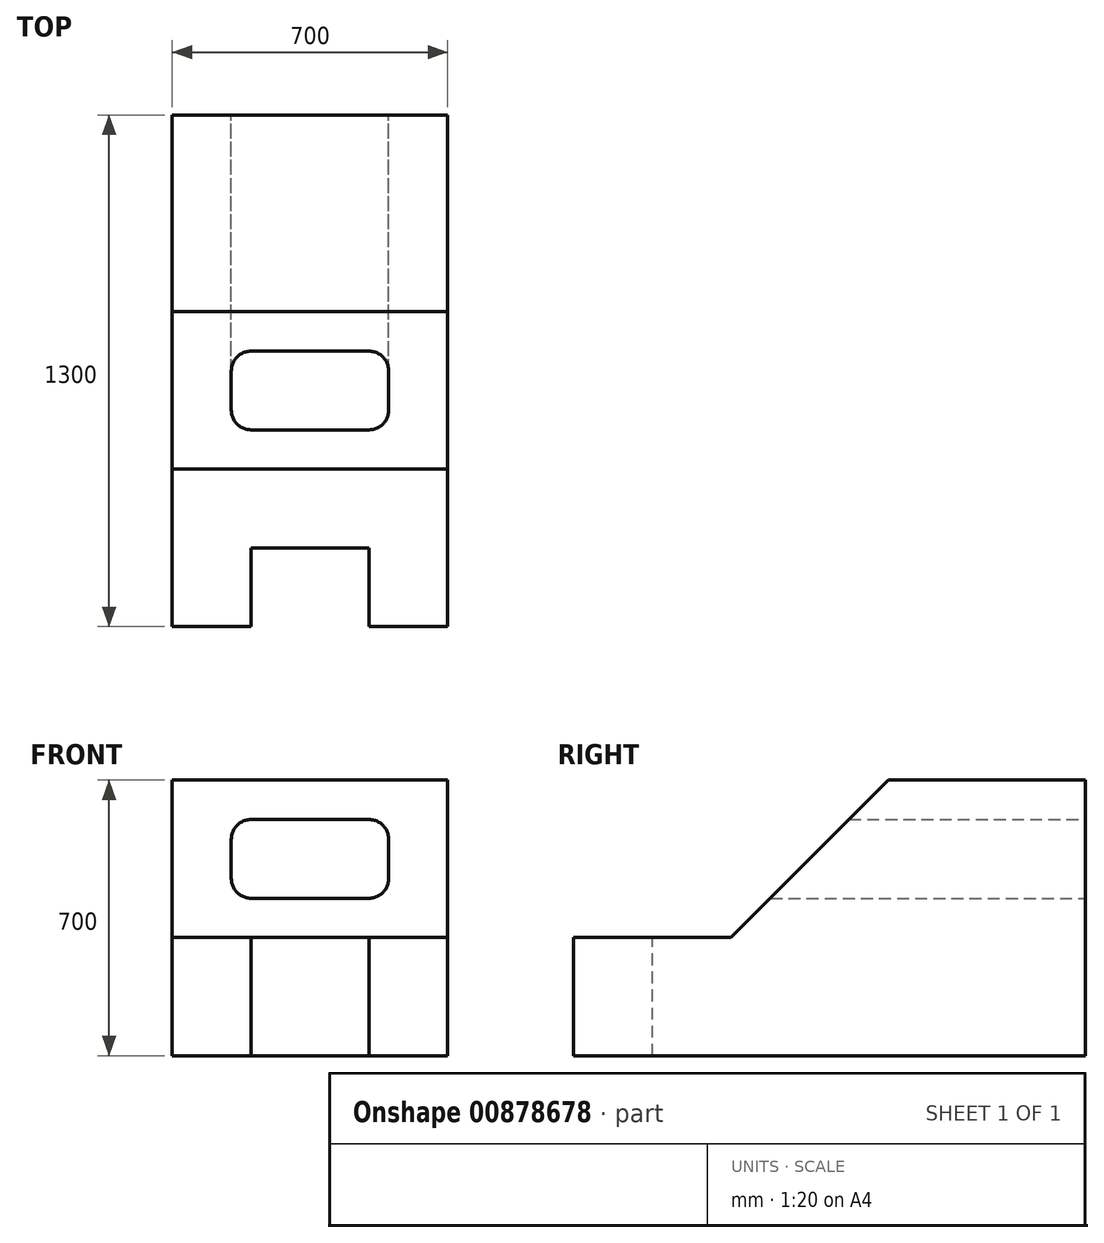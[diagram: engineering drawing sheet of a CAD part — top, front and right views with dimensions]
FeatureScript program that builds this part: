
annotation { "Feature Type Name" : "Feature", "Feature Type Description" : "" }
export const myFeature = defineFeature(function(context is Context, id is Id, definition is map)
    precondition{}
    {
        {
            var Q0;
            Q0=qCreatedBy(makeId("Front.planeOp"),FACE);
            var sketch = newSketch(context, id + "F0", { "sketchPlane" : qUnion([Q0])});
            skLineSegment(sketch, "E0.bottom", {"start": v(350, 350) * mm, "end": v(-350, 350) * mm});
            skLineSegment(sketch, "E0.top", {"start": v(350, -350) * mm, "end": v(-350, -350) * mm});
            skLineSegment(sketch, "E0.left", {"start": v(350, 350) * mm, "end": v(350, -350) * mm});
            skLineSegment(sketch, "E0.right", {"start": v(-350, 350) * mm, "end": v(-350, -350) * mm});
            skPoint(sketch, "E0.middle", {"position": v(0, 0) * mm});
            skSolve(sketch);
        }
        {
            var Q0;
            Q0=makeQuery(id+"F0.imprint","IMPRINT",FACE,{"disambiguationData":[TD([[makeQuery(id+"F0.imprint","IMPRINT",EDGE,{"derivedFrom":sQuery(id+"F0.wireOp",EDGE,"E0.bottom")}),1.0]])]});
            extrude(context, id + "F1", {"entities" : qUnion([Q0]), "depth" : 1300 * mm, "offsetDistance" : 25.4 * mm});
        }
        {
            var Q0;
            Q0=makeQuery(id+"F1.opExtrude","SWEPT_FACE",FACE,{"disambiguationData":[OSD([sQuery(id+"F0.wireOp",EDGE,"E0.left")])]});
            var sketch = newSketch(context, id + "F2", { "sketchPlane" : qUnion([Q0])});
            skLineSegment(sketch, "E1", {"start": v(-500, 350) * mm, "end": v(-900, -50) * mm});
            skLineSegment(sketch, "E2", {"start": v(-900, -50) * mm, "end": v(-1300, -50) * mm});
            skSolve(sketch);
        }
        {
            var Q0;
            {var subQ0=sQuery(id+"F2.wireOp",EDGE,"E1");Q0=makeQuery(id+"F2.imprint","IMPRINT",FACE,{"disambiguationData":[TD([[makeQuery(id+"F2.imprint","IMPRINT",EDGE,{"derivedFrom":subQ0}),-1.0]])]});}
            extrude(context, id + "F3", {"entities" : qUnion([Q0]), "operationType" : NewBodyOperationType.ADD, "endBound" : BoundingType.THROUGH_ALL, "depth" : 25.4 * mm, "offsetDistance" : 25.4 * mm});
        }
        {
            var Q0;
            Q0=makeQuery(id+"F3.opExtrude","CAP_FACE",FACE,{"disambiguationData":[OSD([sQuery(id+"F0.wireOp",EDGE,"E0.bottom"),sQuery(id+"F0.wireOp",EDGE,"E0.left"),sQuery(id+"F2.wireOp",EDGE,"E1"),sQuery(id+"F2.wireOp",EDGE,"E2")])],"isStart":false});
            extrude(context, id + "F4", {"entities" : qUnion([Q0]), "operationType" : NewBodyOperationType.ADD, "endBound" : BoundingType.THROUGH_ALL, "depth" : 25.4 * mm, "offsetDistance" : 25.4 * mm});
        }
        {
            var Q0;
            Q0=makeQuery(id+"F4.opExtrude","CAP_FACE",FACE,{"disambiguationData":[OSD([sQuery(id+"F0.wireOp",EDGE,"E0.bottom"),sQuery(id+"F0.wireOp",EDGE,"E0.left"),sQuery(id+"F2.wireOp",EDGE,"E1"),sQuery(id+"F2.wireOp",EDGE,"E2")])],"isStart":false});
            var sketch = newSketch(context, id + "F5", { "sketchPlane" : qUnion([Q0])});
            skSolve(sketch);
        }
        {
            var Q0;
            Q0 = qSketchRegion(id + "F5", true);
            var Q1;
            Q1=makeQuery(id+"F5.imprint","IMPRINT",FACE,{"disambiguationData":[TD([[makeQuery(id+"F5.imprint","IMPRINT",EDGE,{"derivedFrom":makeQuery(id+"F4.opExtrude","CAP_EDGE",EDGE,{"disambiguationData":[OSD([sQuery(id+"F2.wireOp",EDGE,"E1")])],"isStart":false})}),-1.0]])]});
            extrude(context, id + "F6", {"entities" : qUnion([Q0, Q1]), "operationType" : NewBodyOperationType.REMOVE, "endBound" : BoundingType.THROUGH_ALL, "oppositeDirection" : true, "depth" : 25.4 * mm, "offsetDistance" : 25.4 * mm});
        }
        {
            var Q0;
            Q0=makeQuery(id+"F6.boolean.opBoolean","COPY",FACE,{"derivedFrom":makeQuery(id+"F6.opExtrude","SWEPT_FACE",FACE,{"disambiguationData":[OSD([sQuery(id+"F2.wireOp",EDGE,"E2")])]})});
            var sketch = newSketch(context, id + "F7", { "sketchPlane" : qUnion([Q0])});
            skLineSegment(sketch, "E3.bottom", {"start": v(150, -1100) * mm, "end": v(-150, -1100) * mm});
            skLineSegment(sketch, "E3.top", {"start": v(150, -1500) * mm, "end": v(-150, -1500) * mm});
            skLineSegment(sketch, "E3.left", {"start": v(150, -1100) * mm, "end": v(150, -1500) * mm});
            skLineSegment(sketch, "E3.right", {"start": v(-150, -1100) * mm, "end": v(-150, -1500) * mm});
            skPoint(sketch, "E3.middle", {"position": v(0, -1300) * mm});
            skSolve(sketch);
        }
        {
            var Q0;
            Q0 = qSketchRegion(id + "F7", true);
            extrude(context, id + "F8", {"entities" : qUnion([Q0]), "operationType" : NewBodyOperationType.REMOVE, "endBound" : BoundingType.THROUGH_ALL, "oppositeDirection" : true, "depth" : 25.4 * mm, "offsetDistance" : 25.4 * mm});
        }
        {
            var Q0;
            Q0=makeQuery(id+"F1.opExtrude","CAP_FACE",FACE,{"disambiguationData":[OSD([sQuery(id+"F0.wireOp",EDGE,"E0.bottom"),sQuery(id+"F0.wireOp",EDGE,"E0.top"),sQuery(id+"F0.wireOp",EDGE,"E0.left"),sQuery(id+"F0.wireOp",EDGE,"E0.right")])],"isStart":true});
            var sketch = newSketch(context, id + "F9", { "sketchPlane" : qUnion([Q0])});
            skLineSegment(sketch, "E4.bottom", {"start": v(-200, 250) * mm, "end": v(200, 250) * mm});
            skLineSegment(sketch, "E4.top", {"start": v(-200, 50) * mm, "end": v(200, 50) * mm});
            skLineSegment(sketch, "E4.left", {"start": v(-200, 250) * mm, "end": v(-200, 50) * mm});
            skLineSegment(sketch, "E4.right", {"start": v(200, 250) * mm, "end": v(200, 50) * mm});
            skSolve(sketch);
        }
        {
            var Q0;
            Q0=makeQuery(id+"F9.imprint","IMPRINT",FACE,{"disambiguationData":[TD([[makeQuery(id+"F9.imprint","IMPRINT",EDGE,{"derivedFrom":sQuery(id+"F9.wireOp",EDGE,"E4.bottom")}),-1.0]])]});
            extrude(context, id + "F10", {"entities" : qUnion([Q0]), "operationType" : NewBodyOperationType.REMOVE, "endBound" : BoundingType.THROUGH_ALL, "oppositeDirection" : true, "depth" : 25.4 * mm, "offsetDistance" : 25.4 * mm});
        }
        {
            var Q0;
            Q0=makeQuery(id+"F10.boolean.opBoolean","COPY",EDGE,{"derivedFrom":makeQuery(id+"F10.opExtrude","SWEPT_EDGE",EDGE,{"disambiguationData":[OSD([sQuery(id+"F9.wireOp",EDGE,"E4.bottom"),sQuery(id+"F9.wireOp",EDGE,"E4.left")])]})});
            var Q1;
            Q1=makeQuery(id+"F10.boolean.opBoolean","COPY",EDGE,{"derivedFrom":makeQuery(id+"F10.opExtrude","SWEPT_EDGE",EDGE,{"disambiguationData":[OSD([sQuery(id+"F9.wireOp",EDGE,"E4.top"),sQuery(id+"F9.wireOp",EDGE,"E4.left")])]})});
            var Q2;
            Q2=makeQuery(id+"F10.boolean.opBoolean","COPY",EDGE,{"derivedFrom":makeQuery(id+"F10.opExtrude","SWEPT_EDGE",EDGE,{"disambiguationData":[OSD([sQuery(id+"F9.wireOp",EDGE,"E4.bottom"),sQuery(id+"F9.wireOp",EDGE,"E4.right")])]})});
            var Q3;
            Q3=makeQuery(id+"F10.boolean.opBoolean","COPY",EDGE,{"derivedFrom":makeQuery(id+"F10.opExtrude","SWEPT_EDGE",EDGE,{"disambiguationData":[OSD([sQuery(id+"F9.wireOp",EDGE,"E4.top"),sQuery(id+"F9.wireOp",EDGE,"E4.right")])]})});
            fillet(context, id + "F11", {"entities" : qUnion([Q0, Q1, Q2, Q3]), "radius" : 50 * mm, "tangentPropagation" : true, "allowEdgeOverflow" : false});
        }
    });
